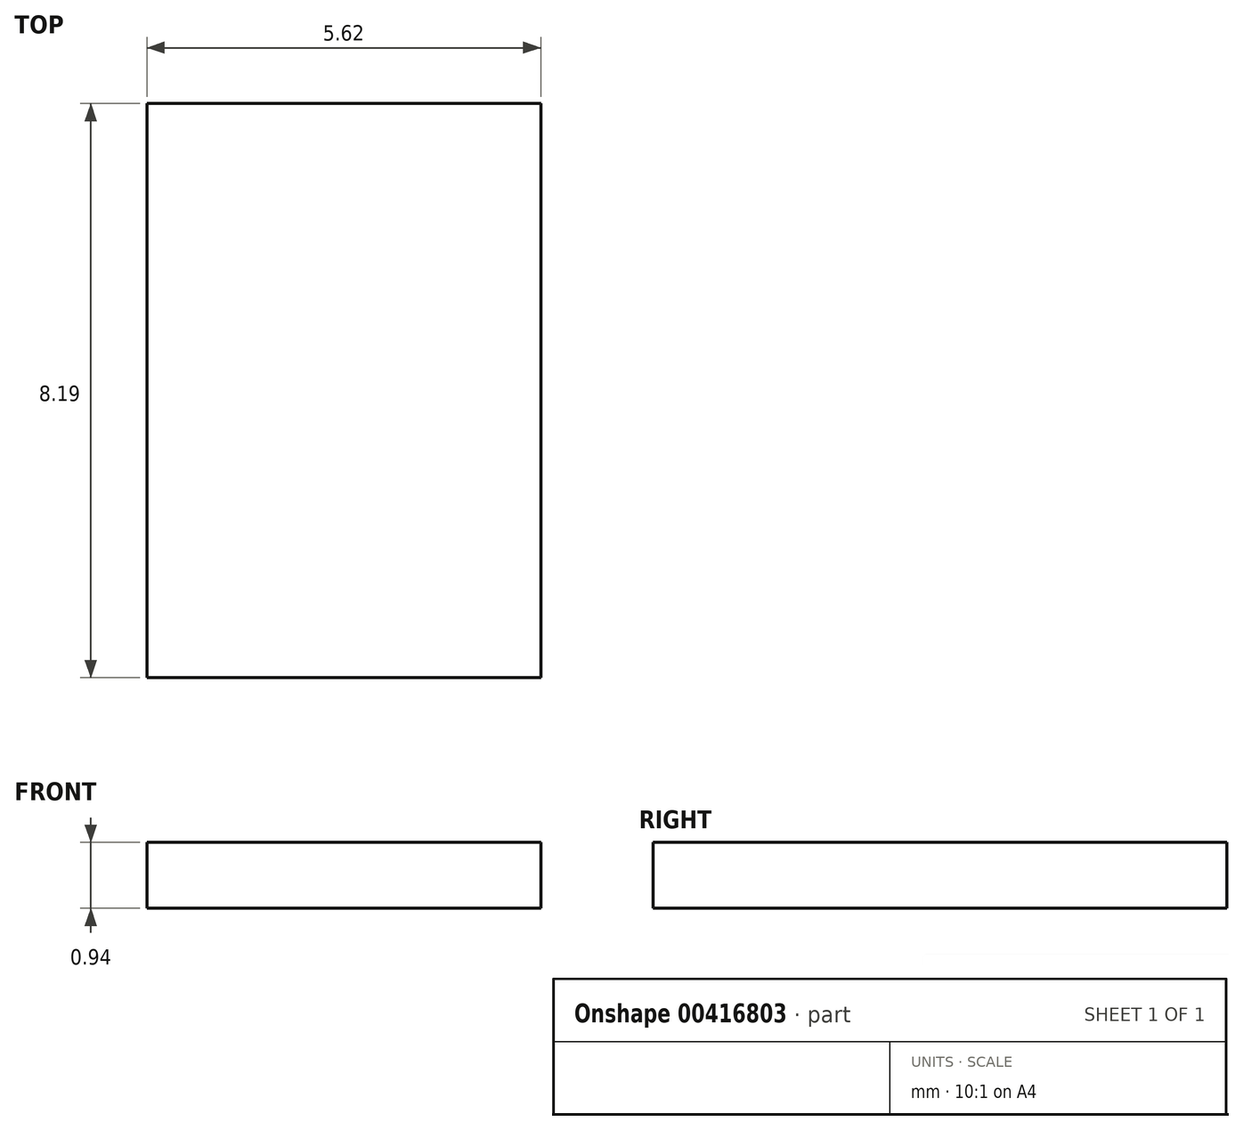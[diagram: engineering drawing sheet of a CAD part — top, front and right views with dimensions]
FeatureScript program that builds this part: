
annotation { "Feature Type Name" : "Feature", "Feature Type Description" : "" }
export const myFeature = defineFeature(function(context is Context, id is Id, definition is map)
    precondition{}
    {
        {
            var Q0;
            Q0=qCreatedBy(makeId("Top.planeOp"),FACE);
            var sketch = newSketch(context, id + "F0", { "sketchPlane" : qUnion([Q0])});
            skLineSegment(sketch, "E0.bottom", {"start": v(0, 0) * mm, "end": v(5.62, 0) * mm});
            skLineSegment(sketch, "E0.top", {"start": v(0, 8.19) * mm, "end": v(5.62, 8.19) * mm});
            skLineSegment(sketch, "E0.left", {"start": v(0, 0) * mm, "end": v(0, 8.19) * mm});
            skLineSegment(sketch, "E0.right", {"start": v(5.62, 0) * mm, "end": v(5.62, 8.19) * mm});
            skSolve(sketch);
        }
        {
            var Q0;
            Q0 = qSketchRegion(id + "F0", true);
            extrude(context, id + "F1", {"entities" : qUnion([Q0]), "depth" : .94 * mm, "offsetDistance" : 25.4 * mm});
        }
    });
